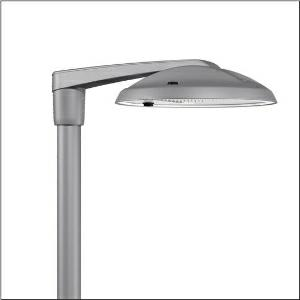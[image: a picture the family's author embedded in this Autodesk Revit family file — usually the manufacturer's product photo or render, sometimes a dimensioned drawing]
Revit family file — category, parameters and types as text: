
# Revit family: dl_r__50_iq_mini___st1_0a_5xa248d31y08ne_98a7
name_source: partatom
category: Lighting Fixtures
units: mm (PartAtom-declared; Revit-internal decimal feet)

## family parameters
Cut with Voids When Loaded = No
Host = Face
Light Source = No
Part Type = Normal
Room Calculation Point = No
Round Connector Dimension = Use Diameter
Shared = No

## types (1)
- --- (1 x LED, 17900 lm, 110.1 W, 3000K)
    Apparent Load = 110 VA
    CIE Flux Codes = 37 72 97 100 100
    Color Rendering = 70
    Color Temperature = 3000K
    Default Elevation = 1800 mm
    Description = DL® 50 iQ mini, mast luminaire, primary light control with lens, of PMMA, primary optical cover: cover, of toughened safety glass, transparent, light distribution: ST1.0a, light emission: direct distribution, primary light characteristic: asymmetric, installation type: post-top, side-entry, LED, High Power LED, rated luminous flux: 17.900lm, luminous efficacy: 163lm/W, light colour: 730, colour temperature: 3000K, control gear: iQ-Street Remote, D4i with power reduction, control: optimised constant luminous flux control (CLO 2.0), Desk-Remote (wireless, voltage-free reading and setting of iQ features in the workshop via application-optimized NFC function/RFID function), Light-Fading, Smart-Wire, Night-Set, Lumen-Switch, Temp-Guard, Auto-Match, Street-Remote, pre-setting: logarithmic dimming characteristic, mains connection: 230..240V, AC, 50/60Hz, connection cable pre-assembled, cable length: 10,5m, start of lifetime: 110W, end of service life: 116W, reduction: 50W, luminaire housing, of diecast aluminium, powder-coated, Siteco® metallic grey (DB 702S), inclination adjustable: 0°, 5°, 10° (post-top) | 0°, -5°, -10°, -15° (side-entry), please order mast post-top element or mast side-entry element separately, diameter: 500mm, height: 115mm, post-top: for spigot size d x l = 76 x 100mm; with reducer (optional accessory) 60 x 100mm | side-entry: for spigot size d x l = 60 x 100mm; with reducer (optional accessory) 42 x 100mm, mounting height: 4..6m, Smart Interface below and above, protection rating (complete): IP66, insulation class (complete): insulation class II (safety insulation), certification: CE, ENEC, ENEC+, VDE, impact resistance: IK08, permissible operating ambient temperature for outdoor applications: -25..+40°C, standard-compliant lighting for roads and squares, packaging unit: 1 piece

Light Distribution: ST1.0a
    Height = 115 mm
    Lamp = 1 x LED
    Lamp Light Flux = 17900 lm
    Lamp Power = 110.1 W
    Lamp count = 1
    Length = 500 mm
    Luminous efficacy = 163 lm/W
    Manufacturer = Siteco
    ModVariant = No
    Model = 5XA248D31Y08NE
    Number of Poles = 1
    OnlyDefault = Yes
    Power Factor = 1
    Product Name = DL® 50 iQ mini | ST1.0a
    Product group = mast luminaire | pylon top
    ProductGroupID = 6100
    Protection Class = Protection class II
    Protection Degree = IP 66
    RLX_Detail_Level = 1
    RLX_Emergency_Light_Flux = 0 lm
    RLX_Emergency_Type = 0
    RLX_Emergency_Type_DB = No
    RlxData = <blob elided: 107209 chars, md5=b0b296be>
    Socket = socket
    Standby Power = 0 W
    System Light Flux = 17900 lm
    System Power = 110 W
    Type Comments = factory setting: luminous flux: 100 % | dim-lin: 254 | 601 mA
    Type Image = l_1251786.jpg
    URL = http://relux.com
    VarID = @adj_065362
    Voltage = 0 V
    Weight = 0.00 kg
    Width = 0 mm  [stored 0 ft]

note: [stored X ft] marks values corroborated as IEEE doubles in the binary element streams (Revit-internal decimal feet)

## geometry (parser evidence)
native form markers: Blend x4, Sweep x9
no freeform markers — native parametric forms only
